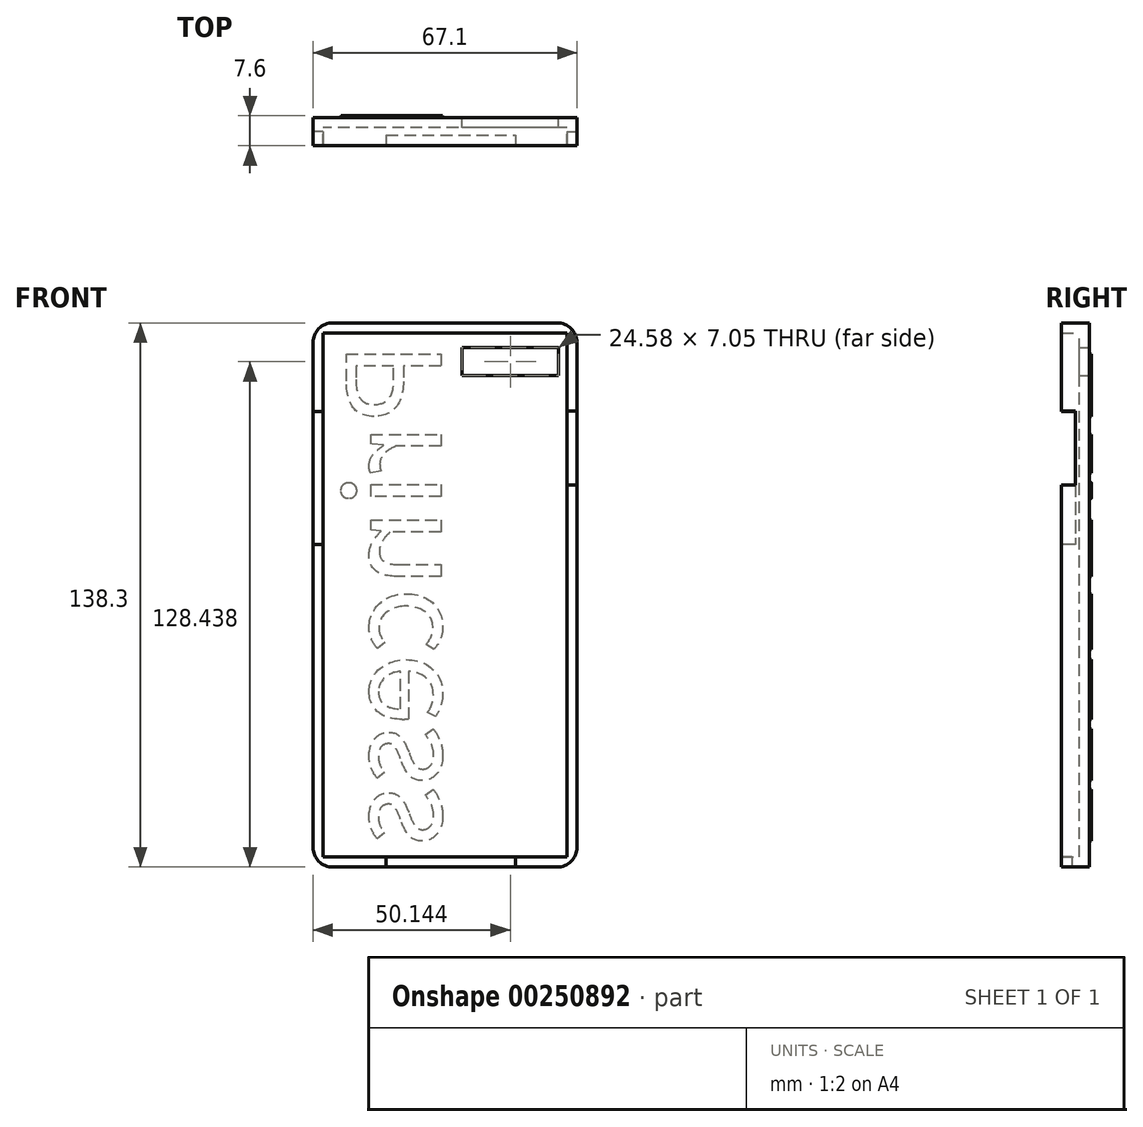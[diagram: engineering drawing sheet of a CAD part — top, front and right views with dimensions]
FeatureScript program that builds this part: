
annotation { "Feature Type Name" : "Feature", "Feature Type Description" : "" }
export const myFeature = defineFeature(function(context is Context, id is Id, definition is map)
    precondition{}
    {
        {
            var Q0;
            Q0=qCreatedBy(makeId("Front.planeOp"),FACE);
            var sketch = newSketch(context, id + "F0", { "sketchPlane" : qUnion([Q0])});
            skLineSegment(sketch, "E0.bottom", {"start": v(33.55, -69.15) * mm, "end": v(-33.55, -69.15) * mm});
            skLineSegment(sketch, "E0.top", {"start": v(33.55, 69.15) * mm, "end": v(-33.55, 69.15) * mm});
            skLineSegment(sketch, "E0.left", {"start": v(33.55, -69.15) * mm, "end": v(33.55, 69.15) * mm});
            skLineSegment(sketch, "E0.right", {"start": v(-33.55, -69.15) * mm, "end": v(-33.55, 69.15) * mm});
            skPoint(sketch, "E0.middle", {"position": v(0, 0) * mm});
            skSolve(sketch);
        }
        {
            var Q0;
            Q0=makeQuery(id+"F0.imprint","IMPRINT",FACE,{"disambiguationData":[TD([[makeQuery(id+"F0.imprint","IMPRINT",EDGE,{"derivedFrom":sQuery(id+"F0.wireOp",EDGE,"E0.bottom")}),-1.0]])]});
            extrude(context, id + "F1", {"entities" : qUnion([Q0]), "endBound" : BoundingType.SYMMETRIC, "depth" : 7.1 * mm});
        }
        {
            var Q0;
            Q0=makeQuery(id+"F1.opExtrude","CAP_FACE",FACE,{"disambiguationData":[OSD([sQuery(id+"F0.wireOp",EDGE,"E0.bottom"),sQuery(id+"F0.wireOp",EDGE,"E0.top"),sQuery(id+"F0.wireOp",EDGE,"E0.left"),sQuery(id+"F0.wireOp",EDGE,"E0.right")])],"isStart":false});
            shell(context, id + "F2", {"entities" : qUnion([Q0]), "thickness" : 2.54 * mm});
        }
        {
            var Q0;
            Q0=makeQuery(id+"F1.opExtrude","SWEPT_EDGE",EDGE,{"disambiguationData":[OSD([sQuery(id+"F0.wireOp",EDGE,"E0.top"),sQuery(id+"F0.wireOp",EDGE,"E0.left")])]});
            var Q1;
            Q1=makeQuery(id+"F1.opExtrude","SWEPT_EDGE",EDGE,{"disambiguationData":[OSD([sQuery(id+"F0.wireOp",EDGE,"E0.bottom"),sQuery(id+"F0.wireOp",EDGE,"E0.left")])]});
            var Q2;
            Q2=makeQuery(id+"F1.opExtrude","SWEPT_EDGE",EDGE,{"disambiguationData":[OSD([sQuery(id+"F0.wireOp",EDGE,"E0.top"),sQuery(id+"F0.wireOp",EDGE,"E0.right")])]});
            var Q3;
            Q3=makeQuery(id+"F1.opExtrude","SWEPT_EDGE",EDGE,{"disambiguationData":[OSD([sQuery(id+"F0.wireOp",EDGE,"E0.bottom"),sQuery(id+"F0.wireOp",EDGE,"E0.right")])]});
            fillet(context, id + "F3", {"entities" : qUnion([Q0, Q1, Q2, Q3]), "radius" : 5.08 * mm, "tangentPropagation" : true, "allowEdgeOverflow" : false});
        }
        {
            var Q0;
            Q0=makeQuery(id+"F2.opShell","OFFSET_FACE",FACE,{"disambiguationData":[OSD([sQuery(id+"F0.wireOp",EDGE,"E0.bottom"),sQuery(id+"F0.wireOp",EDGE,"E0.top"),sQuery(id+"F0.wireOp",EDGE,"E0.left"),sQuery(id+"F0.wireOp",EDGE,"E0.right")])]});
            var sketch = newSketch(context, id + "F4", { "sketchPlane" : qUnion([Q0])});
            skLineSegment(sketch, "E1.bottom", {"start": v(4.3, 62.81) * mm, "end": v(28.88, 62.81) * mm});
            skLineSegment(sketch, "E1.top", {"start": v(4.3, 55.76) * mm, "end": v(28.88, 55.76) * mm});
            skLineSegment(sketch, "E1.left", {"start": v(4.3, 62.81) * mm, "end": v(4.3, 55.76) * mm});
            skLineSegment(sketch, "E1.right", {"start": v(28.88, 62.81) * mm, "end": v(28.88, 55.76) * mm});
            skSolve(sketch);
        }
        {
            var Q0;
            Q0=makeQuery(id+"F4.imprint","IMPRINT",FACE,{"disambiguationData":[TD([[makeQuery(id+"F4.imprint","IMPRINT",EDGE,{"derivedFrom":sQuery(id+"F4.wireOp",EDGE,"E1.bottom")}),-1.0]])]});
            extrude(context, id + "F5", {"entities" : qUnion([Q0]), "operationType" : NewBodyOperationType.REMOVE, "endBound" : BoundingType.SYMMETRIC, "depth" : 25 * mm});
        }
        {
            var Q0;
            Q0=makeQuery(id+"F1.opExtrude","SWEPT_FACE",FACE,{"disambiguationData":[OSD([sQuery(id+"F0.wireOp",EDGE,"E0.bottom")])]});
            var sketch = newSketch(context, id + "F6", { "sketchPlane" : qUnion([Q0])});
            skLineSegment(sketch, "E2.bottom", {"start": v(-14.94, 0.89) * mm, "end": v(17.85, 0.89) * mm});
            skLineSegment(sketch, "E2.top", {"start": v(-14.94, 4.5) * mm, "end": v(17.85, 4.5) * mm});
            skLineSegment(sketch, "E2.left", {"start": v(-14.94, 0.89) * mm, "end": v(-14.94, 4.5) * mm});
            skLineSegment(sketch, "E2.right", {"start": v(17.85, 0.89) * mm, "end": v(17.85, 4.5) * mm});
            skSolve(sketch);
        }
        {
            var Q0;
            Q0=makeQuery(id+"F6.imprint","IMPRINT",FACE,{"disambiguationData":[TD([[makeQuery(id+"F6.imprint","IMPRINT",EDGE,{"derivedFrom":sQuery(id+"F6.wireOp",EDGE,"E2.bottom")}),1.0]])]});
            extrude(context, id + "F7", {"entities" : qUnion([Q0]), "operationType" : NewBodyOperationType.REMOVE, "endBound" : BoundingType.SYMMETRIC, "oppositeDirection" : true, "depth" : 25 * mm});
        }
        {
            var Q0;
            Q0=makeQuery(id+"F1.opExtrude","SWEPT_FACE",FACE,{"disambiguationData":[OSD([sQuery(id+"F0.wireOp",EDGE,"E0.right")])]});
            var sketch = newSketch(context, id + "F8", { "sketchPlane" : qUnion([Q0])});
            skLineSegment(sketch, "E3.bottom", {"start": v(0, 46.62) * mm, "end": v(3.55, 46.62) * mm});
            skLineSegment(sketch, "E3.top", {"start": v(0, 12.77) * mm, "end": v(3.55, 12.77) * mm});
            skLineSegment(sketch, "E3.left", {"start": v(0, 46.62) * mm, "end": v(0, 12.77) * mm});
            skLineSegment(sketch, "E3.right", {"start": v(3.55, 46.62) * mm, "end": v(3.55, 12.77) * mm});
            skSolve(sketch);
        }
        {
            var Q0;
            Q0=makeQuery(id+"F8.imprint","IMPRINT",FACE,{"disambiguationData":[TD([[makeQuery(id+"F8.imprint","IMPRINT",EDGE,{"derivedFrom":sQuery(id+"F8.wireOp",EDGE,"E3.bottom")}),-1.0]])]});
            extrude(context, id + "F9", {"entities" : qUnion([Q0]), "operationType" : NewBodyOperationType.REMOVE, "endBound" : BoundingType.SYMMETRIC, "oppositeDirection" : true, "depth" : 25 * mm});
        }
        {
            var Q0;
            Q0=makeQuery(id+"F1.opExtrude","SWEPT_FACE",FACE,{"disambiguationData":[OSD([sQuery(id+"F0.wireOp",EDGE,"E0.left")])]});
            var sketch = newSketch(context, id + "F10", { "sketchPlane" : qUnion([Q0])});
            skLineSegment(sketch, "E4.bottom", {"start": v(-3.55, 46.8) * mm, "end": v(0, 46.8) * mm});
            skLineSegment(sketch, "E4.top", {"start": v(-3.55, 27.88) * mm, "end": v(0, 27.88) * mm});
            skLineSegment(sketch, "E4.left", {"start": v(-3.55, 46.8) * mm, "end": v(-3.55, 27.88) * mm});
            skLineSegment(sketch, "E4.right", {"start": v(0, 46.8) * mm, "end": v(0, 27.88) * mm});
            skSolve(sketch);
        }
        {
            var Q0;
            Q0=makeQuery(id+"F10.imprint","IMPRINT",FACE,{"disambiguationData":[TD([[makeQuery(id+"F10.imprint","IMPRINT",EDGE,{"derivedFrom":sQuery(id+"F10.wireOp",EDGE,"E4.bottom")}),-1.0]])]});
            extrude(context, id + "F11", {"entities" : qUnion([Q0]), "operationType" : NewBodyOperationType.REMOVE, "oppositeDirection" : true, "depth" : 25 * mm});
        }
        {
            var Q0;
            Q0=makeQuery(id+"F1.opExtrude","CAP_FACE",FACE,{"disambiguationData":[OSD([sQuery(id+"F0.wireOp",EDGE,"E0.bottom"),sQuery(id+"F0.wireOp",EDGE,"E0.top"),sQuery(id+"F0.wireOp",EDGE,"E0.left"),sQuery(id+"F0.wireOp",EDGE,"E0.right")])],"isStart":true});
            var sketch = newSketch(context, id + "F12", { "sketchPlane" : qUnion([Q0])});
            skText(sketch, "E5", { "text": "Princess", "fontName": "NotoSansCJKtc-Regular.otf"});
            const initialGuessF12  = {"E5": [0.001, 0.06456, 0, -1, 0.02365]};
            skSetInitialGuess(sketch, initialGuessF12);
            skSolve(sketch);
        }
        {
            var Q0;
            Q0 = qSketchRegion(id + "F12", true);
            extrude(context, id + "F13", {"entities" : qUnion([Q0]), "operationType" : NewBodyOperationType.ADD, "depth" : .5 * mm});
        }
    });
